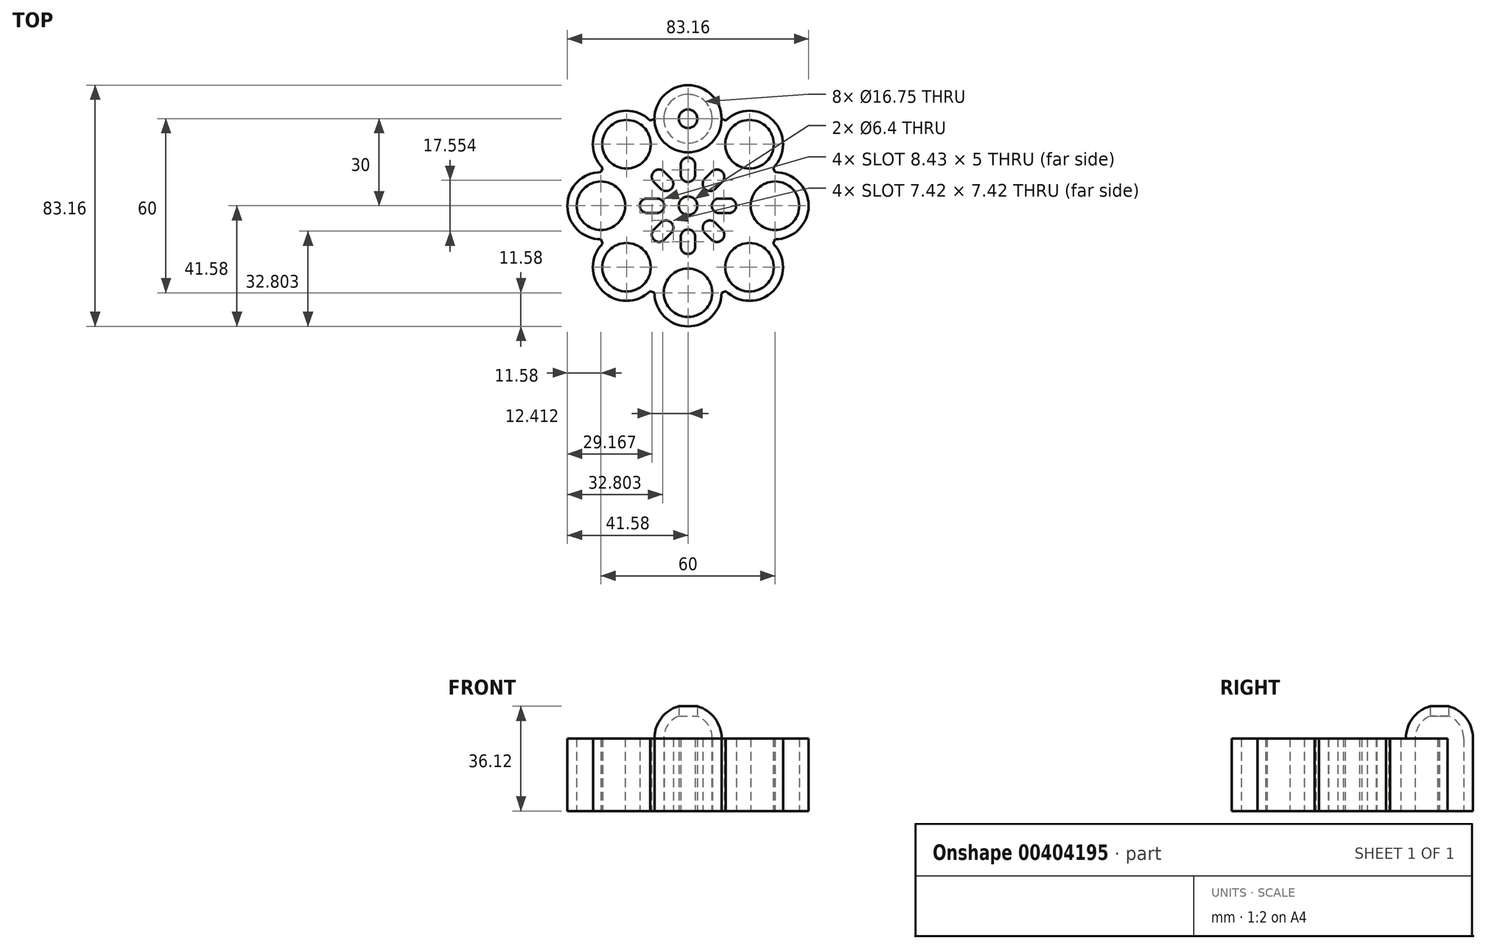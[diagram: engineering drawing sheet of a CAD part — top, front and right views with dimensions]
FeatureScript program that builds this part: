
annotation { "Feature Type Name" : "Feature", "Feature Type Description" : "" }
export const myFeature = defineFeature(function(context is Context, id is Id, definition is map)
    precondition{}
    {
        {
            var Q0;
            Q0=qCreatedBy(makeId("Top.planeOp"),FACE);
            var sketch = newSketch(context, id + "F0", { "sketchPlane" : qUnion([Q0])});
            skCircle(sketch, "E0", {"center": v(0, 0) * mm, "radius": 3.2 * mm});
            skCircle(sketch, "E1", {"center": v(0, 30) * mm, "radius": 8.38 * mm});
            skCircle(sketch, "E2.1.0", {"center": v(-21.21, 21.21) * mm, "radius": 8.38 * mm});
            skCircle(sketch, "E2.2.0", {"center": v(-30, 0) * mm, "radius": 8.38 * mm});
            skCircle(sketch, "E2.3.0", {"center": v(-21.21, -21.21) * mm, "radius": 8.38 * mm});
            skCircle(sketch, "E2.4.0", {"center": v(0, -30) * mm, "radius": 8.38 * mm});
            skCircle(sketch, "E2.5.0", {"center": v(21.21, -21.21) * mm, "radius": 8.38 * mm});
            skCircle(sketch, "E2.6.0", {"center": v(30, 0) * mm, "radius": 8.38 * mm});
            skCircle(sketch, "E2.7.0", {"center": v(21.21, 21.21) * mm, "radius": 8.38 * mm});
            skArc(sketch, "E3", {"start": v(11.58, 30) * mm, "mid": v(0, 41.58) * mm, "end": v(-11.58, 30) * mm});
            skArc(sketch, "E4.1.0", {"start": v(-13.03, 29.4) * mm, "mid": v(-29.4, 29.4) * mm, "end": v(-29.4, 13.03) * mm});
            skArc(sketch, "E4.2.0", {"start": v(-30, 11.58) * mm, "mid": v(-41.58, 0) * mm, "end": v(-30, -11.57) * mm});
            skArc(sketch, "E4.3.0", {"start": v(-29.4, -13.03) * mm, "mid": v(-29.4, -29.4) * mm, "end": v(-13.03, -29.4) * mm});
            skArc(sketch, "E4.4.0", {"start": v(-11.58, -30) * mm, "mid": v(0, -41.58) * mm, "end": v(11.57, -30) * mm});
            skArc(sketch, "E4.5.0", {"start": v(13.03, -29.4) * mm, "mid": v(29.4, -29.4) * mm, "end": v(29.4, -13.03) * mm});
            skArc(sketch, "E4.6.0", {"start": v(30, -11.58) * mm, "mid": v(41.58, 0) * mm, "end": v(30, 11.57) * mm});
            skArc(sketch, "E4.7.0", {"start": v(29.4, 13.03) * mm, "mid": v(29.4, 29.4) * mm, "end": v(13.03, 29.4) * mm});
            skLineSegment(sketch, "E5", {"start": v(11.58, 30) * mm, "end": v(13.03, 29.4) * mm});
            skLineSegment(sketch, "E6", {"start": v(-13.03, 29.4) * mm, "end": v(-11.58, 30) * mm});
            skLineSegment(sketch, "E7", {"start": v(-29.4, 13.03) * mm, "end": v(-30, 11.58) * mm});
            skLineSegment(sketch, "E8", {"start": v(-30, -11.57) * mm, "end": v(-29.4, -13.03) * mm});
            skLineSegment(sketch, "E9", {"start": v(-13.03, -29.4) * mm, "end": v(-11.58, -30) * mm});
            skLineSegment(sketch, "E10", {"start": v(11.57, -30) * mm, "end": v(13.03, -29.4) * mm});
            skLineSegment(sketch, "E11", {"start": v(30, -11.58) * mm, "end": v(29.4, -13.03) * mm});
            skLineSegment(sketch, "E12", {"start": v(29.4, 13.03) * mm, "end": v(30, 11.57) * mm});
            skLineSegment(sketch, "E13.bottom", {"start": v(0, 8.2) * mm, "end": v(0, 8.2) * mm});
            skLineSegment(sketch, "E13.top", {"start": v(0, 16.62) * mm, "end": v(0, 16.62) * mm});
            skLineSegment(sketch, "E13.left", {"start": v(2.5, 10.7) * mm, "end": v(2.5, 14.12) * mm});
            skLineSegment(sketch, "E13.right", {"start": v(-2.5, 10.7) * mm, "end": v(-2.5, 14.12) * mm});
            skPoint(sketch, "E13.middle", {"position": v(0, 12.41) * mm});
            skPoint(sketch, "E14.visualSharp", {"position": v(-2.5, 16.62) * mm});
            skArc(sketch, "E14.filletArc", {"start": v(0, 16.62) * mm, "mid": v(-1.77, 15.9) * mm, "end": v(-2.5, 14.12) * mm});
            skPoint(sketch, "E15.visualSharp", {"position": v(-2.5, 8.2) * mm});
            skArc(sketch, "E15.filletArc", {"start": v(-2.5, 10.7) * mm, "mid": v(-1.77, 8.93) * mm, "end": v(0, 8.2) * mm});
            skPoint(sketch, "E16.visualSharp", {"position": v(2.5, 8.2) * mm});
            skArc(sketch, "E16.filletArc", {"start": v(0, 8.2) * mm, "mid": v(1.77, 8.93) * mm, "end": v(2.5, 10.7) * mm});
            skPoint(sketch, "E17.visualSharp", {"position": v(2.5, 16.62) * mm});
            skArc(sketch, "E17.filletArc", {"start": v(2.5, 14.12) * mm, "mid": v(1.77, 15.9) * mm, "end": v(0, 16.62) * mm});
            skPoint(sketch, "E18.1.0", {"position": v(-4.03, 7.57) * mm});
            skLineSegment(sketch, "E18.1.1", {"start": v(-9.33, 5.8) * mm, "end": v(-11.76, 8.22) * mm});
            skLineSegment(sketch, "E18.1.2", {"start": v(-5.8, 9.33) * mm, "end": v(-8.22, 11.76) * mm});
            skPoint(sketch, "E18.1.3", {"position": v(-13.52, 9.99) * mm});
            skArc(sketch, "E18.1.4", {"start": v(-11.76, 11.76) * mm, "mid": v(-12.49, 9.99) * mm, "end": v(-11.76, 8.22) * mm});
            skArc(sketch, "E18.1.5", {"start": v(-5.8, 5.8) * mm, "mid": v(-5.07, 7.57) * mm, "end": v(-5.8, 9.33) * mm});
            skArc(sketch, "E18.1.6", {"start": v(-9.33, 5.8) * mm, "mid": v(-7.57, 5.07) * mm, "end": v(-5.8, 5.8) * mm});
            skArc(sketch, "E18.1.7", {"start": v(-8.22, 11.76) * mm, "mid": v(-9.99, 12.49) * mm, "end": v(-11.76, 11.76) * mm});
            skPoint(sketch, "E18.1.8", {"position": v(-9.99, 13.52) * mm});
            skPoint(sketch, "E18.1.9", {"position": v(-8.78, 8.78) * mm});
            skPoint(sketch, "E18.1.10", {"position": v(-7.57, 4.03) * mm});
            skPoint(sketch, "E18.2.0", {"position": v(-8.2, 2.5) * mm});
            skLineSegment(sketch, "E18.2.1", {"start": v(-10.7, -2.5) * mm, "end": v(-14.12, -2.5) * mm});
            skLineSegment(sketch, "E18.2.2", {"start": v(-10.7, 2.5) * mm, "end": v(-14.12, 2.5) * mm});
            skPoint(sketch, "E18.2.3", {"position": v(-16.62, -2.5) * mm});
            skArc(sketch, "E18.2.4", {"start": v(-16.62, 0) * mm, "mid": v(-15.9, -1.77) * mm, "end": v(-14.12, -2.5) * mm});
            skArc(sketch, "E18.2.5", {"start": v(-8.2, 0) * mm, "mid": v(-8.93, 1.77) * mm, "end": v(-10.7, 2.5) * mm});
            skArc(sketch, "E18.2.6", {"start": v(-10.7, -2.5) * mm, "mid": v(-8.93, -1.77) * mm, "end": v(-8.2, 0) * mm});
            skArc(sketch, "E18.2.7", {"start": v(-14.12, 2.5) * mm, "mid": v(-15.9, 1.77) * mm, "end": v(-16.62, 0) * mm});
            skPoint(sketch, "E18.2.8", {"position": v(-16.62, 2.5) * mm});
            skPoint(sketch, "E18.2.9", {"position": v(-12.41, 0) * mm});
            skPoint(sketch, "E18.2.10", {"position": v(-8.2, -2.5) * mm});
            skPoint(sketch, "E18.3.0", {"position": v(-7.57, -4.03) * mm});
            skLineSegment(sketch, "E18.3.1", {"start": v(-5.8, -9.33) * mm, "end": v(-8.22, -11.76) * mm});
            skLineSegment(sketch, "E18.3.2", {"start": v(-9.33, -5.8) * mm, "end": v(-11.76, -8.22) * mm});
            skPoint(sketch, "E18.3.3", {"position": v(-9.99, -13.52) * mm});
            skArc(sketch, "E18.3.4", {"start": v(-11.76, -11.76) * mm, "mid": v(-9.99, -12.49) * mm, "end": v(-8.22, -11.76) * mm});
            skArc(sketch, "E18.3.5", {"start": v(-5.8, -5.8) * mm, "mid": v(-7.57, -5.07) * mm, "end": v(-9.33, -5.8) * mm});
            skArc(sketch, "E18.3.6", {"start": v(-5.8, -9.33) * mm, "mid": v(-5.07, -7.57) * mm, "end": v(-5.8, -5.8) * mm});
            skArc(sketch, "E18.3.7", {"start": v(-11.76, -8.22) * mm, "mid": v(-12.49, -9.99) * mm, "end": v(-11.76, -11.76) * mm});
            skPoint(sketch, "E18.3.8", {"position": v(-13.52, -9.99) * mm});
            skPoint(sketch, "E18.3.9", {"position": v(-8.78, -8.78) * mm});
            skPoint(sketch, "E18.3.10", {"position": v(-4.03, -7.57) * mm});
            skPoint(sketch, "E18.4.0", {"position": v(-2.5, -8.2) * mm});
            skLineSegment(sketch, "E18.4.1", {"start": v(2.5, -10.7) * mm, "end": v(2.5, -14.12) * mm});
            skLineSegment(sketch, "E18.4.2", {"start": v(-2.5, -10.7) * mm, "end": v(-2.5, -14.12) * mm});
            skPoint(sketch, "E18.4.3", {"position": v(2.5, -16.62) * mm});
            skArc(sketch, "E18.4.4", {"start": v(0, -16.62) * mm, "mid": v(1.77, -15.9) * mm, "end": v(2.5, -14.12) * mm});
            skArc(sketch, "E18.4.5", {"start": v(0, -8.2) * mm, "mid": v(-1.77, -8.93) * mm, "end": v(-2.5, -10.7) * mm});
            skArc(sketch, "E18.4.6", {"start": v(2.5, -10.7) * mm, "mid": v(1.77, -8.93) * mm, "end": v(0, -8.2) * mm});
            skArc(sketch, "E18.4.7", {"start": v(-2.5, -14.12) * mm, "mid": v(-1.77, -15.9) * mm, "end": v(0, -16.62) * mm});
            skPoint(sketch, "E18.4.8", {"position": v(-2.5, -16.62) * mm});
            skPoint(sketch, "E18.4.9", {"position": v(0, -12.41) * mm});
            skPoint(sketch, "E18.4.10", {"position": v(2.5, -8.2) * mm});
            skPoint(sketch, "E18.5.0", {"position": v(4.03, -7.57) * mm});
            skLineSegment(sketch, "E18.5.1", {"start": v(9.33, -5.8) * mm, "end": v(11.76, -8.22) * mm});
            skLineSegment(sketch, "E18.5.2", {"start": v(5.8, -9.33) * mm, "end": v(8.22, -11.76) * mm});
            skPoint(sketch, "E18.5.3", {"position": v(13.52, -9.99) * mm});
            skArc(sketch, "E18.5.4", {"start": v(11.76, -11.76) * mm, "mid": v(12.49, -9.99) * mm, "end": v(11.76, -8.22) * mm});
            skArc(sketch, "E18.5.5", {"start": v(5.8, -5.8) * mm, "mid": v(5.07, -7.57) * mm, "end": v(5.8, -9.33) * mm});
            skArc(sketch, "E18.5.6", {"start": v(9.33, -5.8) * mm, "mid": v(7.57, -5.07) * mm, "end": v(5.8, -5.8) * mm});
            skArc(sketch, "E18.5.7", {"start": v(8.22, -11.76) * mm, "mid": v(9.99, -12.49) * mm, "end": v(11.76, -11.76) * mm});
            skPoint(sketch, "E18.5.8", {"position": v(9.99, -13.52) * mm});
            skPoint(sketch, "E18.5.9", {"position": v(8.78, -8.78) * mm});
            skPoint(sketch, "E18.5.10", {"position": v(7.57, -4.03) * mm});
            skPoint(sketch, "E18.6.0", {"position": v(8.2, -2.5) * mm});
            skLineSegment(sketch, "E18.6.1", {"start": v(10.7, 2.5) * mm, "end": v(14.12, 2.5) * mm});
            skLineSegment(sketch, "E18.6.2", {"start": v(10.7, -2.5) * mm, "end": v(14.12, -2.5) * mm});
            skPoint(sketch, "E18.6.3", {"position": v(16.62, 2.5) * mm});
            skArc(sketch, "E18.6.4", {"start": v(16.62, 0) * mm, "mid": v(15.9, 1.77) * mm, "end": v(14.12, 2.5) * mm});
            skArc(sketch, "E18.6.5", {"start": v(8.2, 0) * mm, "mid": v(8.93, -1.77) * mm, "end": v(10.7, -2.5) * mm});
            skArc(sketch, "E18.6.6", {"start": v(10.7, 2.5) * mm, "mid": v(8.93, 1.77) * mm, "end": v(8.2, 0) * mm});
            skArc(sketch, "E18.6.7", {"start": v(14.12, -2.5) * mm, "mid": v(15.9, -1.77) * mm, "end": v(16.62, 0) * mm});
            skPoint(sketch, "E18.6.8", {"position": v(16.62, -2.5) * mm});
            skPoint(sketch, "E18.6.9", {"position": v(12.41, 0) * mm});
            skPoint(sketch, "E18.6.10", {"position": v(8.2, 2.5) * mm});
            skPoint(sketch, "E18.7.0", {"position": v(7.57, 4.03) * mm});
            skLineSegment(sketch, "E18.7.1", {"start": v(5.8, 9.33) * mm, "end": v(8.22, 11.76) * mm});
            skLineSegment(sketch, "E18.7.2", {"start": v(9.33, 5.8) * mm, "end": v(11.76, 8.22) * mm});
            skPoint(sketch, "E18.7.3", {"position": v(9.99, 13.52) * mm});
            skArc(sketch, "E18.7.4", {"start": v(11.76, 11.76) * mm, "mid": v(9.99, 12.49) * mm, "end": v(8.22, 11.76) * mm});
            skArc(sketch, "E18.7.5", {"start": v(5.8, 5.8) * mm, "mid": v(7.57, 5.07) * mm, "end": v(9.33, 5.8) * mm});
            skArc(sketch, "E18.7.6", {"start": v(5.8, 9.33) * mm, "mid": v(5.07, 7.57) * mm, "end": v(5.8, 5.8) * mm});
            skArc(sketch, "E18.7.7", {"start": v(11.76, 8.22) * mm, "mid": v(12.49, 9.99) * mm, "end": v(11.76, 11.76) * mm});
            skPoint(sketch, "E18.7.8", {"position": v(13.52, 9.99) * mm});
            skPoint(sketch, "E18.7.9", {"position": v(8.78, 8.78) * mm});
            skPoint(sketch, "E18.7.10", {"position": v(4.03, 7.57) * mm});
            skSolve(sketch);
        }
        {
            var Q0;
            Q0 = qSketchRegion(id + "F0", true);
            extrude(context, id + "F1", {"entities" : qUnion([Q0]), "depth" : 25 * mm});
        }
        {
            var Q0;
            Q0=makeQuery(id+"F1.opExtrude","CAP_FACE",FACE,{"disambiguationData":[OSD([sQuery(id+"F0.wireOp",EDGE,"E0"),sQuery(id+"F0.wireOp",EDGE,"E1"),sQuery(id+"F0.wireOp",EDGE,"E2.1.0"),sQuery(id+"F0.wireOp",EDGE,"E2.2.0"),sQuery(id+"F0.wireOp",EDGE,"E2.3.0"),sQuery(id+"F0.wireOp",EDGE,"E2.4.0"),sQuery(id+"F0.wireOp",EDGE,"E2.5.0"),sQuery(id+"F0.wireOp",EDGE,"E2.6.0"),sQuery(id+"F0.wireOp",EDGE,"E2.7.0"),sQuery(id+"F0.wireOp",EDGE,"E3"),sQuery(id+"F0.wireOp",EDGE,"E4.1.0"),sQuery(id+"F0.wireOp",EDGE,"E4.2.0"),sQuery(id+"F0.wireOp",EDGE,"E4.3.0"),sQuery(id+"F0.wireOp",EDGE,"E4.4.0"),sQuery(id+"F0.wireOp",EDGE,"E4.5.0"),sQuery(id+"F0.wireOp",EDGE,"E4.6.0"),sQuery(id+"F0.wireOp",EDGE,"E4.7.0"),sQuery(id+"F0.wireOp",EDGE,"E5"),sQuery(id+"F0.wireOp",EDGE,"E6"),sQuery(id+"F0.wireOp",EDGE,"E7"),sQuery(id+"F0.wireOp",EDGE,"E8"),sQuery(id+"F0.wireOp",EDGE,"E9"),sQuery(id+"F0.wireOp",EDGE,"E10"),sQuery(id+"F0.wireOp",EDGE,"E11"),sQuery(id+"F0.wireOp",EDGE,"E12"),sQuery(id+"F0.wireOp",EDGE,"E13.left"),sQuery(id+"F0.wireOp",EDGE,"E13.right"),sQuery(id+"F0.wireOp",EDGE,"E14.filletArc"),sQuery(id+"F0.wireOp",EDGE,"E15.filletArc"),sQuery(id+"F0.wireOp",EDGE,"E16.filletArc"),sQuery(id+"F0.wireOp",EDGE,"E17.filletArc"),sQuery(id+"F0.wireOp",EDGE,"E18.1.1"),sQuery(id+"F0.wireOp",EDGE,"E18.1.2"),sQuery(id+"F0.wireOp",EDGE,"E18.1.4"),sQuery(id+"F0.wireOp",EDGE,"E18.1.5"),sQuery(id+"F0.wireOp",EDGE,"E18.1.6"),sQuery(id+"F0.wireOp",EDGE,"E18.1.7"),sQuery(id+"F0.wireOp",EDGE,"E18.2.1"),sQuery(id+"F0.wireOp",EDGE,"E18.2.2"),sQuery(id+"F0.wireOp",EDGE,"E18.2.4"),sQuery(id+"F0.wireOp",EDGE,"E18.2.5"),sQuery(id+"F0.wireOp",EDGE,"E18.2.6"),sQuery(id+"F0.wireOp",EDGE,"E18.2.7"),sQuery(id+"F0.wireOp",EDGE,"E18.3.1"),sQuery(id+"F0.wireOp",EDGE,"E18.3.2"),sQuery(id+"F0.wireOp",EDGE,"E18.3.4"),sQuery(id+"F0.wireOp",EDGE,"E18.3.5"),sQuery(id+"F0.wireOp",EDGE,"E18.3.6"),sQuery(id+"F0.wireOp",EDGE,"E18.3.7"),sQuery(id+"F0.wireOp",EDGE,"E18.4.1"),sQuery(id+"F0.wireOp",EDGE,"E18.4.2"),sQuery(id+"F0.wireOp",EDGE,"E18.4.4"),sQuery(id+"F0.wireOp",EDGE,"E18.4.5"),sQuery(id+"F0.wireOp",EDGE,"E18.4.6"),sQuery(id+"F0.wireOp",EDGE,"E18.4.7"),sQuery(id+"F0.wireOp",EDGE,"E18.5.1"),sQuery(id+"F0.wireOp",EDGE,"E18.5.2"),sQuery(id+"F0.wireOp",EDGE,"E18.5.4"),sQuery(id+"F0.wireOp",EDGE,"E18.5.5"),sQuery(id+"F0.wireOp",EDGE,"E18.5.6"),sQuery(id+"F0.wireOp",EDGE,"E18.5.7"),sQuery(id+"F0.wireOp",EDGE,"E18.6.1"),sQuery(id+"F0.wireOp",EDGE,"E18.6.2"),sQuery(id+"F0.wireOp",EDGE,"E18.6.4"),sQuery(id+"F0.wireOp",EDGE,"E18.6.5"),sQuery(id+"F0.wireOp",EDGE,"E18.6.6"),sQuery(id+"F0.wireOp",EDGE,"E18.6.7"),sQuery(id+"F0.wireOp",EDGE,"E18.7.1"),sQuery(id+"F0.wireOp",EDGE,"E18.7.2"),sQuery(id+"F0.wireOp",EDGE,"E18.7.4"),sQuery(id+"F0.wireOp",EDGE,"E18.7.5"),sQuery(id+"F0.wireOp",EDGE,"E18.7.6"),sQuery(id+"F0.wireOp",EDGE,"E18.7.7")])],"isStart":false});
            var sketch = newSketch(context, id + "F2", { "sketchPlane" : qUnion([Q0])});
            skArc(sketch, "E19", {"start": v(0, 41.58) * mm, "mid": v(11.58, 30) * mm, "end": v(0, 18.42) * mm});
            skArc(sketch, "E20", {"start": v(0, 38.38) * mm, "mid": v(8.38, 30) * mm, "end": v(0, 21.62) * mm});
            skLineSegment(sketch, "E21", {"start": v(0, 38.38) * mm, "end": v(0, 41.58) * mm});
            skLineSegment(sketch, "E22", {"start": v(0, 21.62) * mm, "end": v(0, 18.42) * mm});
            skSolve(sketch);
        }
        {
            var Q0;
            Q0 = qSketchRegion(id + "F2", true);
            var Q1;
            Q1=sQuery(id+"F2.wireOp",EDGE,"E21");
            revolve(context, id + "F3", {"operationType" : NewBodyOperationType.ADD, "entities" : qUnion([Q0]), "axis" : qUnion([Q1]), "revolveType" : RevolveType.ONE_DIRECTION, "oppositeDirection" : true, "angle" : 180 * degree});
        }
        {
            var Q0;
            Q0=qCreatedBy(makeId("Top.planeOp"),FACE);
            var sketch = newSketch(context, id + "F4", { "sketchPlane" : qUnion([Q0])});
            skCircle(sketch, "E23", {"center": v(0, 30) * mm, "radius": 3.2 * mm});
            skSolve(sketch);
        }
        {
            var Q0;
            Q0 = qSketchRegion(id + "F4", true);
            extrude(context, id + "F5", {"entities" : qUnion([Q0]), "operationType" : NewBodyOperationType.REMOVE, "endBound" : BoundingType.THROUGH_ALL, "depth" : 25 * mm});
        }
    });
